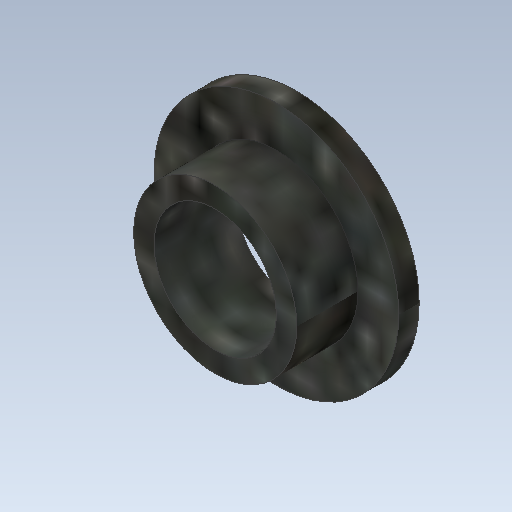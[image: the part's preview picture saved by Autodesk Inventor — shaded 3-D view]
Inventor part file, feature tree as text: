
AUTODESK INVENTOR PART (.ipt)
format: ipt  version: 2020.2 (Build 242310000, 310)  size: 169,472 bytes
history: native  units: mm
features: extrude x2, other x1, sketch x1
ambient origin geometry x8: Origin, YZ Plane, XZ Plane, XY Plane, X Axis, Y Axis, Z Axis, Center Point
bodies: Body1 (feature_tree)
feature tree (4):
  other  "ソリッド1"
  sketch  "スケッチ1"
  extrude  "押し出し1"  Depth=6.0mm
  extrude  "押し出し2"  Depth=8.0mm
